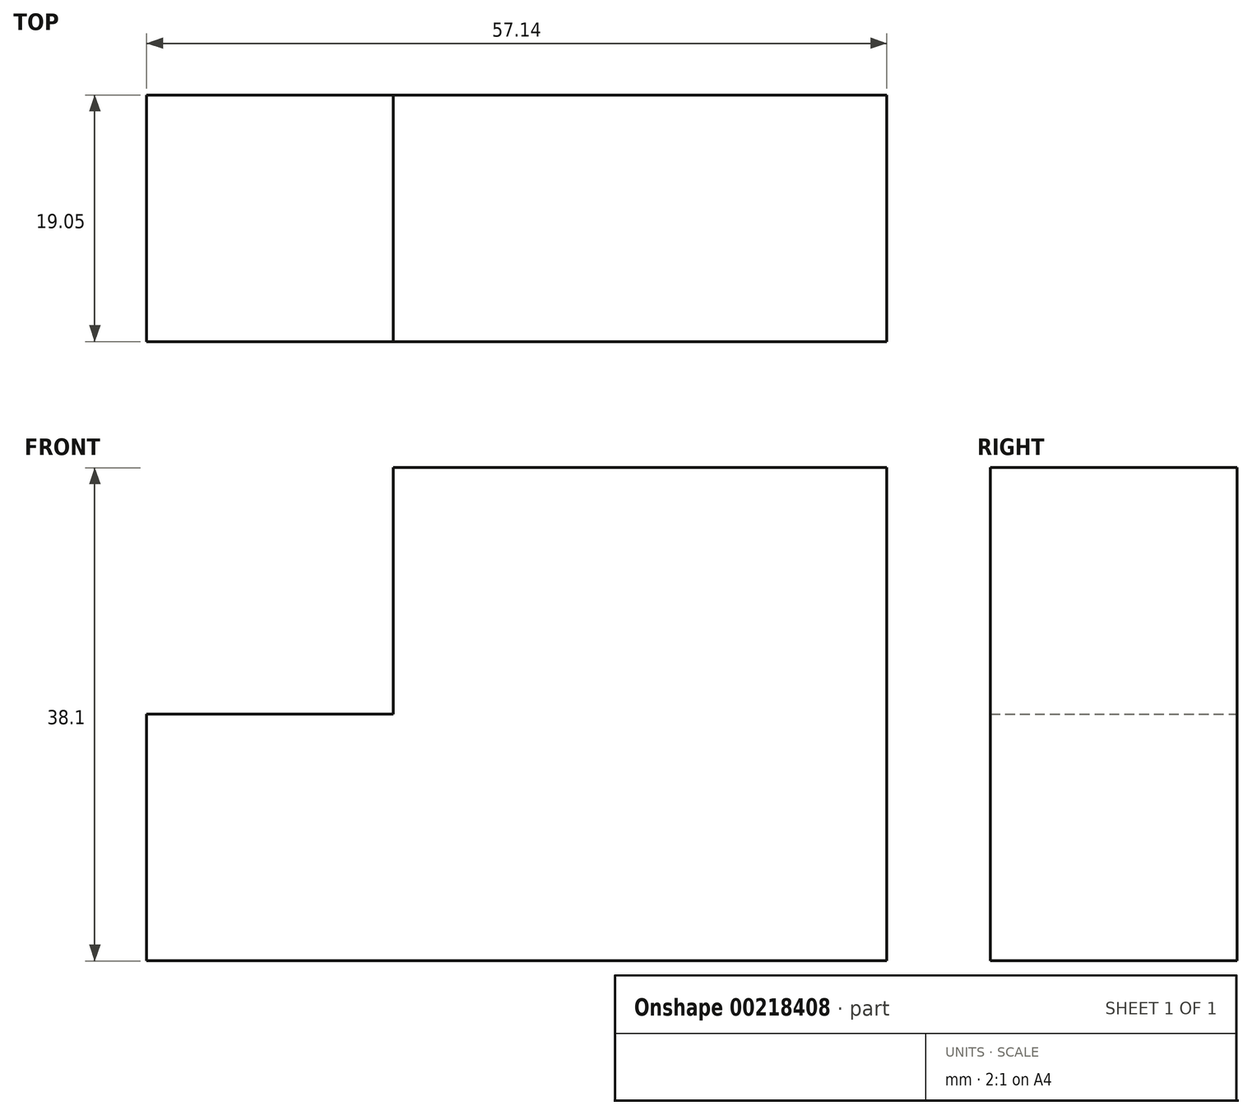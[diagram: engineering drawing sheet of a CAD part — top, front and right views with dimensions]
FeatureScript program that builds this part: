
annotation { "Feature Type Name" : "Feature", "Feature Type Description" : "" }
export const myFeature = defineFeature(function(context is Context, id is Id, definition is map)
    precondition{}
    {
        {
            var Q0;
            Q0=qCreatedBy(makeId("Front.planeOp"),FACE);
            var sketch = newSketch(context, id + "F0", { "sketchPlane" : qUnion([Q0])});
            skLineSegment(sketch, "E0.bottom", {"start": v(9.52, 9.53) * mm, "end": v(-9.53, 9.52) * mm});
            skLineSegment(sketch, "E0.top", {"start": v(9.53, -9.52) * mm, "end": v(-9.52, -9.52) * mm});
            skLineSegment(sketch, "E0.left", {"start": v(9.53, 9.52) * mm, "end": v(9.53, -9.52) * mm});
            skLineSegment(sketch, "E0.right", {"start": v(-9.53, 9.52) * mm, "end": v(-9.52, -9.52) * mm});
            skPoint(sketch, "E0.middle", {"position": v(0, 0) * mm});
            skLineSegment(sketch, "E1", {"start": v(-9.53, 9.52) * mm, "end": v(-28.58, 9.52) * mm});
            skLineSegment(sketch, "E2", {"start": v(-28.58, 9.52) * mm, "end": v(-28.58, -9.53) * mm});
            skLineSegment(sketch, "E3", {"start": v(-28.58, -9.53) * mm, "end": v(-9.52, -9.52) * mm});
            skLineSegment(sketch, "E4", {"start": v(9.53, -9.52) * mm, "end": v(28.58, -9.52) * mm});
            skLineSegment(sketch, "E5", {"start": v(28.58, -9.52) * mm, "end": v(28.57, 9.53) * mm});
            skLineSegment(sketch, "E6", {"start": v(28.58, 9.53) * mm, "end": v(9.52, 9.52) * mm});
            skLineSegment(sketch, "E7", {"start": v(9.52, 9.52) * mm, "end": v(9.52, 28.57) * mm});
            skLineSegment(sketch, "E8", {"start": v(9.52, 28.57) * mm, "end": v(28.57, 28.58) * mm});
            skLineSegment(sketch, "E9", {"start": v(28.57, 28.58) * mm, "end": v(28.58, 9.53) * mm});
            skLineSegment(sketch, "E10", {"start": v(9.52, 28.57) * mm, "end": v(-9.53, 28.57) * mm});
            skLineSegment(sketch, "E11", {"start": v(-9.53, 28.57) * mm, "end": v(-9.53, 9.52) * mm});
            skSolve(sketch);
        }
        {
            var Q0;
            Q0 = qSketchRegion(id + "F0", true);
            extrude(context, id + "F1", {"entities" : qUnion([Q0]), "depth" : 19.05 * mm});
        }
    });
